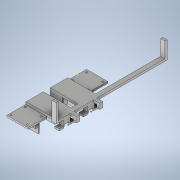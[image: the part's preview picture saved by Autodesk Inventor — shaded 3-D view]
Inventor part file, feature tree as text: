
AUTODESK INVENTOR PART (.ipt)
format: ipt  version: 2020.2 (Build 242310000, 310)  size: 846,336 bytes
history: native  units: mm
features: sketch x35, extrude x35, projected_geometry x17, hole x3
ambient origin geometry x8: Origin, YZ Plane, XZ Plane, XY Plane, X Axis, Y Axis, Z Axis, Center Point
bodies: Solid1 (feature_tree)
feature tree (90):
  sketch  "Sketch1"  dims[d0=8.0mm d1=98.298mm]
  extrude  "Extrusion1"  Depth=98.298mm
  extrude  "Extrusion2"  Depth=4.0mm
  extrude  "Extrusion3"  Depth=4.0mm TaperAngle=0.0deg
  extrude  "Extrusion4"  Depth=34.0mm
  extrude  "Extrusion5"  Depth=12.7mm
  extrude  "Extrusion6"  Depth=25.0mm
  hole  "Hole1"  [1 undecoded]
  extrude  "Extrusion11"  TaperAngle=60.0deg  [1 undecoded]
  extrude  "Extrusion12"  TaperAngle=120.0deg  [1 undecoded]
  sketch  "Sketch16"  dims[d19=6.4262mm d20=120.0deg]
  extrude  "Extrusion13"  Depth=6.4262mm
  extrude  "Extrusion14"  Depth=6.4262mm
  sketch  "Sketch17"  dims[d21=120.0deg d22=6.4262mm]
  extrude  "Extrusion15"  Depth=25.4mm TaperAngle=0.0deg
  extrude  "Extrusion18"  Depth=6.0mm
  extrude  "Extrusion19"  Depth=8.89mm
  extrude  "Extrusion20"  Depth=10.0mm
  hole  "Hole2"  [1 undecoded]
  extrude  "Extrusion21"  Depth=2.0mm
  extrude  "Extrusion22"  Depth=2.0mm
  sketch  "Sketch27"  dims[d45=8.89mm d46=2.0mm]
  extrude  "Extrusion23"  Depth=25.4mm
  extrude  "Extrusion24"  Depth=32.48mm
  extrude  "Extrusion25"  TaperAngle=90.0deg  [1 undecoded]
  sketch  "Sketch29"  dims[d79=51.53mm d80=32.48mm]
  extrude  "Extrusion26"  Depth=2.0mm
  extrude  "Extrusion27"  Depth=21.0mm
  extrude  "Extrusion28"  Depth=36.0mm TaperAngle=0.0deg
  extrude  "Extrusion29"  Depth=8.0mm
  extrude  "Extrusion30"  Depth=17.5mm
  extrude  "Extrusion32"  Depth=35.0mm
  extrude  "Extrusion38"  Depth=5.0mm
  extrude  "Extrusion39"  TaperAngle=90.0deg  [1 undecoded]
  extrude  "Extrusion40"  Depth=5.0mm
  hole  "Hole4"  [1 undecoded]
  extrude  "Extrusion43"  Depth=1.5mm
  extrude  "Extrusion44"  TaperAngle=0.0deg  [1 undecoded]
  extrude  "Extrusion45"  Depth=28.8036mm
  extrude  "Extrusion46"  Depth=12.7mm
  extrude  "Extrusion47"  Depth=12.7mm
  extrude  "Extrusion48"  TaperAngle=120.0deg  [1 undecoded]
  extrude  "Extrusion49"  Depth=12.7mm
  sketch  "Sketch2"  dims[d2=8.0mm d3=4.0mm]
  sketch  "Sketch3"  dims[d4=4.0mm d5=4.0mm d6=0.0mm]
  sketch  "Sketch4"  dims[d7=34.0mm d8=0.0mm d9=19.558mm]
  sketch  "Sketch5"  dims[d10=16.1125mm d11=12.7mm]
  sketch  "Sketch6"  dims[d12=25.0mm d13=0.0mm d14=11.1125mm]
  sketch  "Sketch14"  dims[d15=6.4135mm d16=12.827mm]
  projected_geometry  "Projected Loop2"
  sketch  "Sketch15"  dims[d17=6.4262mm d18=60.0deg]
  projected_geometry  "Projected Loop3"
  sketch  "Sketch18"  dims[d23=120.0deg d24=6.4262mm]
  sketch  "Sketch21"  dims[d25=120.0deg d26=25.4mm d27=0.0mm]
  sketch  "Sketch22"  dims[d28=6.0mm d29=8.89mm]
  sketch  "Sketch23"  dims[d30=5.9944mm d31=8.89mm]
  sketch  "Sketch24"  dims[d32=25.4mm d33=0.0mm d34=10.0mm]
  sketch  "Sketch25"  dims[d35=90.0deg d36=20.0mm]
  projected_geometry  "Projected Loop5"
  sketch  "Sketch26"  dims[d37=3.4mm d38=19.05mm d39=6.2992mm d40=6.35mm d41=90.0deg d42=5.0mm d43=0.0mm d44=2.0mm]
  sketch  "Sketch28"  dims[d47=25.4mm d48=0.0mm d78=16.24mm]
  sketch  "Sketch30"  dims[d81=90.0deg d82=90.0deg]
  sketch  "Sketch32"  dims[d83=4.0mm d84=0.0mm d87=2.0mm]
  projected_geometry  "Projected Loop6"
  sketch  "Sketch33"  dims[d88=2.0mm d89=21.0mm]
  projected_geometry  "Projected Loop7"
  sketch  "Sketch35"  dims[d90=2.0mm d91=36.0mm d92=0.0mm]
  projected_geometry  "Projected Loop8"
  sketch  "Sketch42"  dims[d93=13.878mm d94=8.0mm]
  sketch  "Sketch43"  dims[d95=180.0deg d96=17.5mm]
  projected_geometry  "Projected Loop9"
  projected_geometry  "Projected Loop10"
  projected_geometry  "Projected Loop11"
  projected_geometry  "Projected Loop12"
  sketch  "Sketch44"  dims[d97=90.0deg d98=35.0mm]
  sketch  "Sketch45"  dims[d99=3.5mm d100=5.0mm]
  sketch  "Sketch48"  dims[d101=7.0mm d102=90.0deg]
  sketch  "Sketch49"  dims[d103=5.0mm d104=3.4mm]
  projected_geometry  "Projected Loop13"
  projected_geometry  "Projected Loop14"
  sketch  "Sketch50"  dims[d105=3.4mm d106=25.4mm d107=0.0mm]
  projected_geometry  "Projected Loop15"
  sketch  "Sketch51"  dims[d108=6.4262mm d109=0.0mm d110=1.5mm]
  sketch  "Sketch52"  dims[d111=1.5mm d112=0.0mm d113=0.0mm]
  sketch  "Sketch53"  dims[d128=44.8mm d129=28.8036mm]
  projected_geometry  "Projected Loop16"
  projected_geometry  "Projected Loop17"
  projected_geometry  "Projected Loop18"
  projected_geometry  "Projected Loop19"
  sketch  "Sketch54"  dims[d130=25.4mm d131=0.0mm d132=3.2131mm d133=6.4262mm d134=120.0deg d135=3.2131mm d136=6.4262mm d137=120.0deg d138=25.4mm d139=0.0mm d140=8.001mm d141=13.8938mm d142=8.001mm d143=0.0mm d144=25.4mm d145=0.0mm d146=10.0mm d147=20.0mm d148=3.4mm d149=19.05mm d150=6.2992mm d151=6.35mm d152=90.0deg d153=5.0mm d154=0.0mm d155=16.2433mm d156=32.4866mm d157=51.5366mm d158=4.0mm d159=0.0mm d160=21.0mm d161=2.0mm d162=2.0mm d163=2.0mm d164=2.0mm d165=36.0mm d166=0.0mm d167=7.0mm d168=5.0mm d169=5.0mm d170=17.5mm d171=35.0mm d172=3.4mm d173=3.4mm d174=5.0mm d175=0.0mm d176=5.0mm d177=0.0mm d178=1.5mm d179=1.5mm d180=25.4mm d181=0.0mm d182=19.05mm d183=10.0mm d184=5.08mm d185=4.0mm d186=0.0mm d187=10.0mm d188=0.0mm d189=2.0mm d190=2.0mm d191=25.4mm d192=0.0mm d194=30.0mm d195=0.0mm d196=102.489mm d197=0.0mm d201=11.43mm d202=0.0mm d239=25.4mm d240=0.0mm d241=1.5mm d242=0.0mm d243=39.0mm d244=35.0mm d245=39.0mm d246=35.0mm d247=3.0mm d248=0.0mm d249=5.0mm d250=5.0mm d251=29.7mm d252=26.05mm d253=4.0mm d254=4.0mm d255=29.7mm d256=26.05mm d257=3.4mm d258=19.05mm d259=6.2992mm d260=6.35mm d261=90.0deg d262=25.4mm d263=20.594885mm d271=4.0mm d272=28.4mm d273=0.0mm d274=25.4mm d275=0.0mm d276=3.429mm d277=180.0deg d278=30.0mm d279=0.0mm d280=6.35mm d281=25.4mm d282=0.0mm d283=5.08mm d284=25.4mm d285=0.0mm d286=2.0mm d287=0.0mm d288=12.7mm d289=0.0mm d214=12.7mm d215=0.872665mm d216=12.7mm d217=0.872665mm d228=12.7mm d229=0.872665mm d230=12.7mm d231=0.872665mm]
note: 9 required parameter values undecoded (feature->parameter linkage not recoverable at this tier; creation-order binding heuristic only, values carry confidence <= 0.55)
